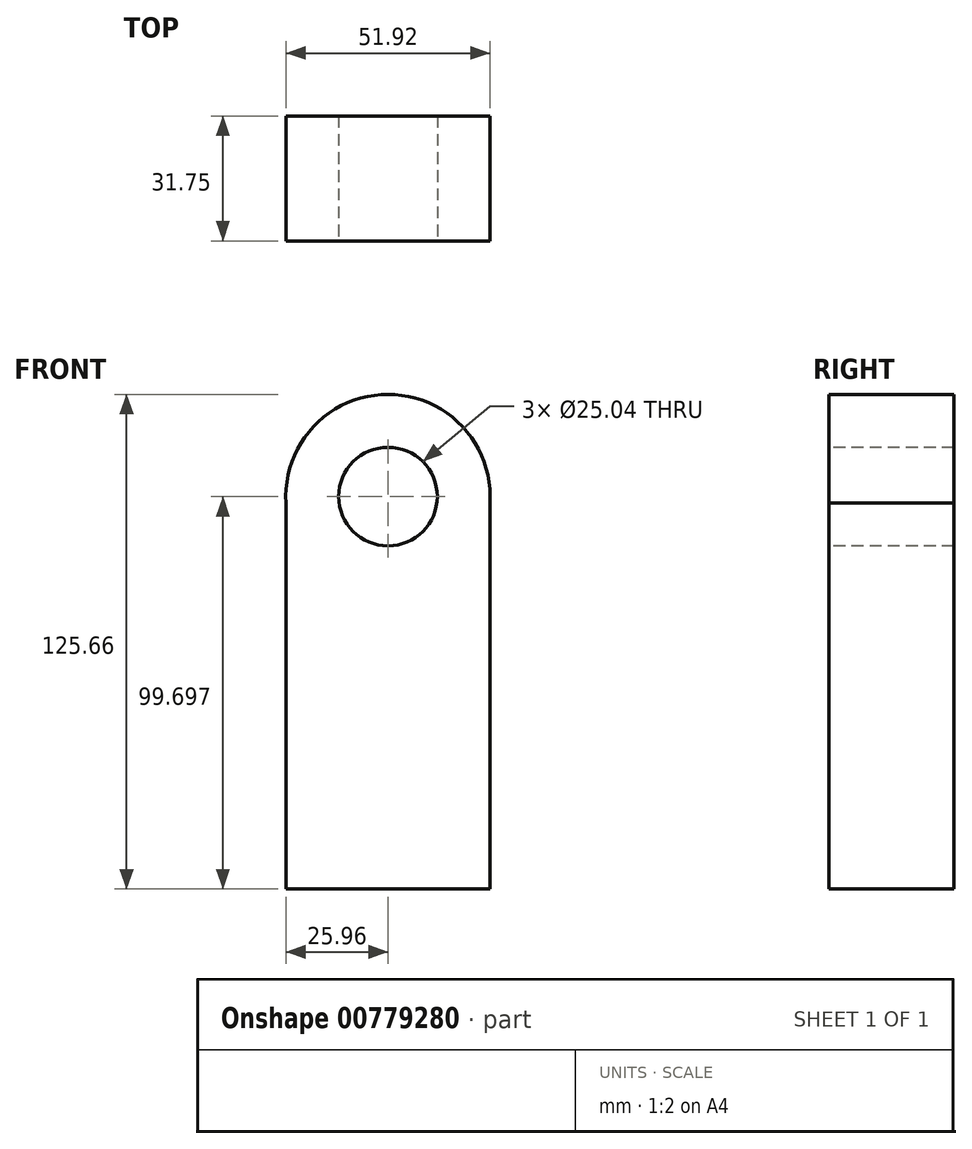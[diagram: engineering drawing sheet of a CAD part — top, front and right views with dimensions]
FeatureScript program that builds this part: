
annotation { "Feature Type Name" : "Feature", "Feature Type Description" : "" }
export const myFeature = defineFeature(function(context is Context, id is Id, definition is map)
    precondition{}
    {
        {
            var Q0;
            Q0=qCreatedBy(makeId("Front.planeOp"),FACE);
            var sketch = newSketch(context, id + "F0", { "sketchPlane" : qUnion([Q0])});
            skLineSegment(sketch, "E0.top", {"start": v(25.91, -49.85) * mm, "end": v(-25.91, -49.85) * mm});
            skLineSegment(sketch, "E0.left", {"start": v(25.91, 49.85) * mm, "end": v(25.91, -49.85) * mm});
            skLineSegment(sketch, "E0.right", {"start": v(-25.91, 49.85) * mm, "end": v(-25.91, -49.85) * mm});
            skPoint(sketch, "E0.middle", {"position": v(0, 0) * mm});
            skPoint(sketch, "E1.middle", {"position": v(25.91, 49.85) * mm});
            skArc(sketch, "E2", {"start": v(25.91, 48.24) * mm, "mid": v(0, 75.81) * mm, "end": v(-25.91, 48.24) * mm});
            skCircle(sketch, "E3", {"center": v(0, 49.85) * mm, "radius": 12.52 * mm});
            skSolve(sketch);
        }
        {
            var Q0;
            {var subQ2=sQuery(id+"F0.wireOp",EDGE,"E0.top");Q0=makeQuery(id+"F0.imprint","IMPRINT",FACE,{"disambiguationData":[TD([[makeQuery(id+"F0.imprint","IMPRINT",EDGE,{"derivedFrom":subQ2}),-1.0]])]});}
            extrude(context, id + "F1", {"entities" : qUnion([Q0]), "oppositeDirection" : true, "depth" : 31.75 * mm, "offsetDistance" : 25.4 * mm});
        }
    });
